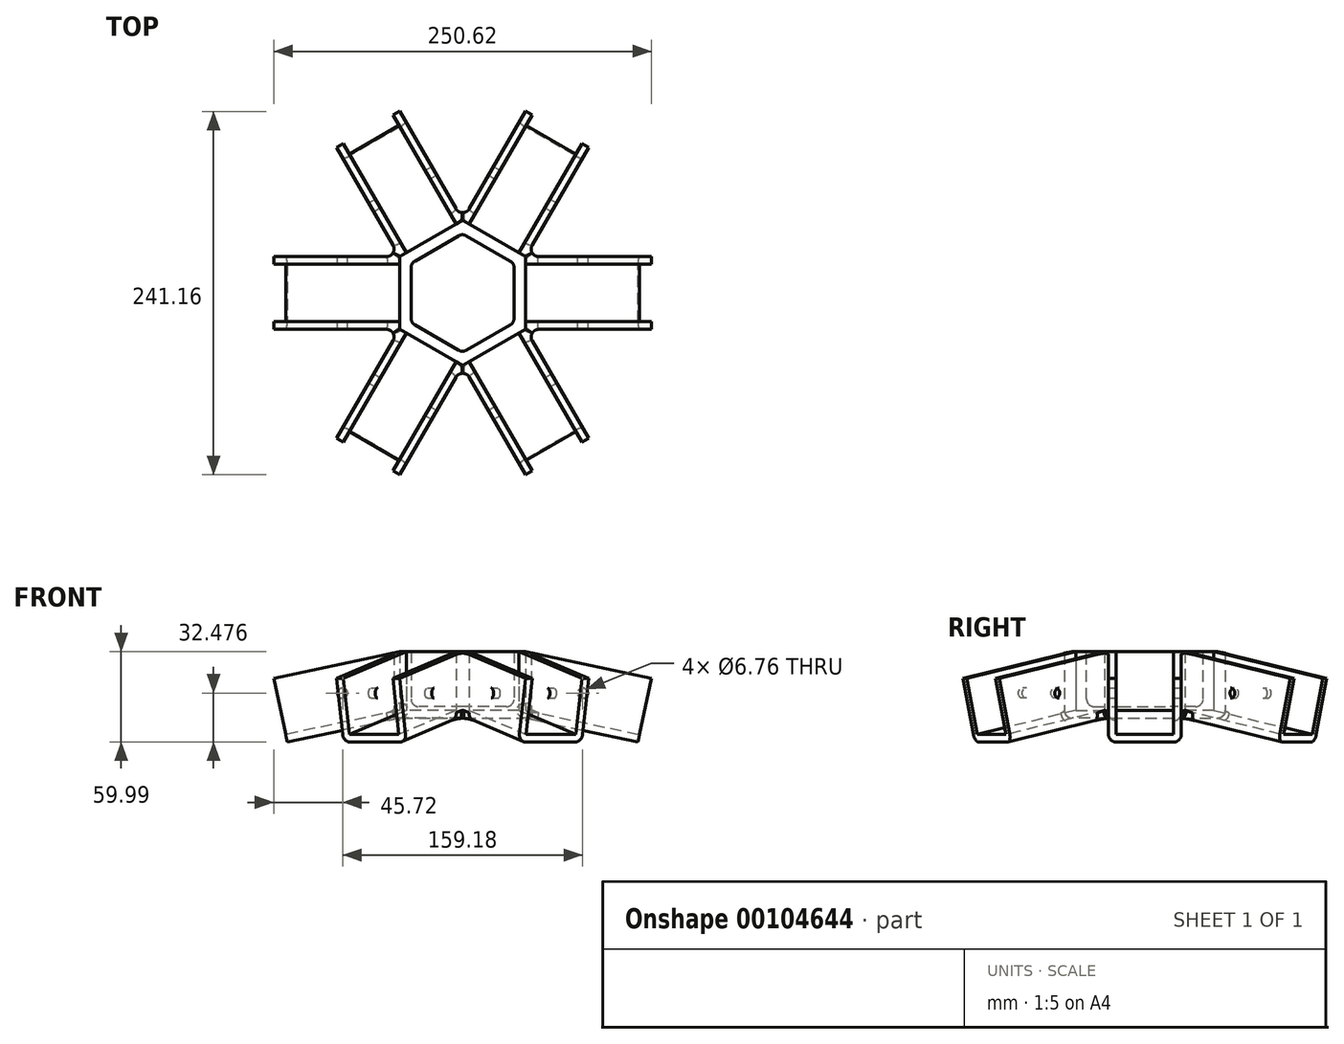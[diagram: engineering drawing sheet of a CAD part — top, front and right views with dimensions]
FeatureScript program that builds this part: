
annotation { "Feature Type Name" : "Feature", "Feature Type Description" : "" }
export const myFeature = defineFeature(function(context is Context, id is Id, definition is map)
    precondition{}
    {
        {
            var Q0;
            Q0=qCreatedBy(makeId("Top.planeOp"),FACE);
            var sketch = newSketch(context, id + "F0", { "sketchPlane" : qUnion([Q0])});
            skCircle(sketch, "E0.cCircle", {"center": v(0, 0) * mm, "radius": 41.8 * mm, "construction": true});
            skLineSegment(sketch, "E0.0", {"start": v(41.8, 24.13) * mm, "end": v(41.8, -24.13) * mm});
            skLineSegment(sketch, "E0.1", {"start": v(41.8, -24.13) * mm, "end": v(0, -48.26) * mm});
            skLineSegment(sketch, "E0.2", {"start": v(0, -48.26) * mm, "end": v(-41.8, -24.13) * mm});
            skLineSegment(sketch, "E0.3", {"start": v(-41.8, -24.13) * mm, "end": v(-41.8, 24.13) * mm});
            skLineSegment(sketch, "E0.4", {"start": v(-41.8, 24.13) * mm, "end": v(0, 48.26) * mm});
            skLineSegment(sketch, "E0.5", {"start": v(0, 48.26) * mm, "end": v(41.8, 24.13) * mm});
            skPoint(sketch, "E0.0.midPoint", {"position": v(41.8, 0) * mm});
            skSolve(sketch);
        }
        {
            var Q0;
            Q0=qSketchRegion(id+"F0",true);
            extrude(context, id + "F1", {"entities" : qUnion([Q0]), "depth" : 44.15 * mm});
        }
        {
            var Q0;
            Q0=qCreatedBy(makeId("Front.planeOp"),FACE);
            var sketch = newSketch(context, id + "F2", { "sketchPlane" : qUnion([Q0])});
            skLineSegment(sketch, "E1", {"start": v(41.8, 0) * mm, "end": v(116.33, -15.84) * mm});
            skLineSegment(sketch, "E2", {"start": v(116.33, -15.84) * mm, "end": v(125.3, 26.4) * mm});
            skLineSegment(sketch, "E3", {"start": v(125.3, 26.4) * mm, "end": v(41.8, 44.15) * mm});
            skLineSegment(sketch, "E4", {"start": v(41.8, 44.15) * mm, "end": v(41.8, 0) * mm});
            skSolve(sketch);
        }
        {
            var Q0;
            Q0=makeQuery(id+"F2.imprint","IMPRINT",FACE,{"disambiguationData":[TD([[makeQuery(id+"F2.imprint","IMPRINT",EDGE,{"derivedFrom":sQuery(id+"F2.wireOp",EDGE,"E1")}),1.0]])]});
            extrude(context, id + "F3", {"entities" : qUnion([Q0]), "endBound" : BoundingType.SYMMETRIC, "depth" : 48.26 * mm});
        }
        {
            var Q0;
            Q0=makeQuery(id+"F3.opExtrude","SWEPT_FACE",FACE,{"disambiguationData":[OSD([sQuery(id+"F2.wireOp",EDGE,"E3")])]});
            var Q1;
            Q1=makeQuery(id+"F3.opExtrude","SWEPT_FACE",FACE,{"disambiguationData":[OSD([sQuery(id+"F2.wireOp",EDGE,"E2")])]});
            var Q2;
            Q2=makeQuery(id+"F3.opExtrude","SWEPT_FACE",FACE,{"disambiguationData":[OSD([sQuery(id+"F2.wireOp",EDGE,"E4")])]});
            shell(context, id + "F4", {"entities" : qUnion([Q0, Q1, Q2]), "thickness" : 5.08 * mm});
        }
        {
            var Q0;
            Q0=makeQuery(id+"F3.opExtrude","CAP_FACE",FACE,{"disambiguationData":[OSD([sQuery(id+"F2.wireOp",EDGE,"E1"),sQuery(id+"F2.wireOp",EDGE,"E2"),sQuery(id+"F2.wireOp",EDGE,"E3"),sQuery(id+"F2.wireOp",EDGE,"E4")])],"isStart":false});
            var sketch = newSketch(context, id + "F5", { "sketchPlane" : qUnion([Q0])});
            skPoint(sketch, "E5", {"position": v(79.59, 16.64) * mm});
            skLineSegment(sketch, "E6", {"start": v(41.8, 44.15) * mm, "end": v(117.39, -10.87) * mm, "construction": true});
            skSolve(sketch);
        }
        {
            var Q0;
            Q0=sQuery(id+"F5.wireOp",VERTEX,"E5");
            var Q1;
            Q1=makeQuery(id+"F3.opExtrude","SWEPT_BODY",BODY,{"disambiguationData":[OSD([sQuery(id+"F2.wireOp",EDGE,"E1"),sQuery(id+"F2.wireOp",EDGE,"E2"),sQuery(id+"F2.wireOp",EDGE,"E3"),sQuery(id+"F2.wireOp",EDGE,"E4")])]});
            hole(context, id + "F6", {"style" : HoleStyle.SIMPLE, "endStyle" : HoleEndStyle.THROUGH, "standardTappedOrClearance" : lookupTablePath({ "standard" : "ANSI", "fit" : "Normal (ASME)", "size" : "1/4", "type" : "Clearance" }), "standardBlindInLast" : lookupTablePath({ "fit" : "Free", "standard" : "ANSI", "size" : "1/4", "type" : "Clearance" }), "holeDiameter" : 6.76 * mm, "locations" : qUnion([Q0]), "scope" : qUnion([Q1]), "isTappedThrough" : true});
        }
        {
            var Q0;
            Q0=qCreatedBy(makeId("Front.planeOp"),FACE);
            var sketch = newSketch(context, id + "F7", { "sketchPlane" : qUnion([Q0])});
            skLineSegment(sketch, "E7", {"start": v(0, 0) * mm, "end": v(0, 66.69) * mm, "construction": true});
            skSolve(sketch);
        }
        {
            var Q0;
            Q0=makeQuery(id+"F3.opExtrude","SWEPT_BODY",BODY,{"disambiguationData":[OSD([sQuery(id+"F2.wireOp",EDGE,"E1"),sQuery(id+"F2.wireOp",EDGE,"E2"),sQuery(id+"F2.wireOp",EDGE,"E3"),sQuery(id+"F2.wireOp",EDGE,"E4")])]});
            var Q1;
            Q1=sQuery(id+"F7.wireOp",EDGE,"E7");
            circularPattern(context, id + "F8", {"entities" : qUnion([Q0]), "axis" : qUnion([Q1]), "angle" : 60 * degree, "instanceCount" : 6});
        }
        {
            var Q0;
            Q0=makeQuery(id+"F1.opExtrude","CAP_FACE",FACE,{"disambiguationData":[OSD([sQuery(id+"F0.wireOp",EDGE,"E0.0"),sQuery(id+"F0.wireOp",EDGE,"E0.1"),sQuery(id+"F0.wireOp",EDGE,"E0.2"),sQuery(id+"F0.wireOp",EDGE,"E0.3"),sQuery(id+"F0.wireOp",EDGE,"E0.4"),sQuery(id+"F0.wireOp",EDGE,"E0.5")])],"isStart":false});
            shell(context, id + "F9", {"entities" : qUnion([Q0]), "thickness" : 7.62 * mm});
        }
        {
            var Q0;
            Q0=makeQuery(id+"F8.opPattern","COPY",BODY,{"derivedFrom":makeQuery(id+"F3.opExtrude","SWEPT_BODY",BODY,{"disambiguationData":[OSD([sQuery(id+"F2.wireOp",EDGE,"E1"),sQuery(id+"F2.wireOp",EDGE,"E2"),sQuery(id+"F2.wireOp",EDGE,"E3"),sQuery(id+"F2.wireOp",EDGE,"E4")])]}),"instanceName":"3"});
            var Q1;
            Q1=makeQuery(id+"F8.opPattern","COPY",BODY,{"derivedFrom":makeQuery(id+"F3.opExtrude","SWEPT_BODY",BODY,{"disambiguationData":[OSD([sQuery(id+"F2.wireOp",EDGE,"E1"),sQuery(id+"F2.wireOp",EDGE,"E2"),sQuery(id+"F2.wireOp",EDGE,"E3"),sQuery(id+"F2.wireOp",EDGE,"E4")])]}),"instanceName":"2"});
            var Q2;
            Q2=makeQuery(id+"F8.opPattern","COPY",BODY,{"derivedFrom":makeQuery(id+"F3.opExtrude","SWEPT_BODY",BODY,{"disambiguationData":[OSD([sQuery(id+"F2.wireOp",EDGE,"E1"),sQuery(id+"F2.wireOp",EDGE,"E2"),sQuery(id+"F2.wireOp",EDGE,"E3"),sQuery(id+"F2.wireOp",EDGE,"E4")])]}),"instanceName":"1"});
            var Q3;
            Q3=makeQuery(id+"F3.opExtrude","SWEPT_BODY",BODY,{"disambiguationData":[OSD([sQuery(id+"F2.wireOp",EDGE,"E1"),sQuery(id+"F2.wireOp",EDGE,"E2"),sQuery(id+"F2.wireOp",EDGE,"E3"),sQuery(id+"F2.wireOp",EDGE,"E4")])]});
            var Q4;
            Q4=makeQuery(id+"F8.opPattern","COPY",BODY,{"derivedFrom":makeQuery(id+"F3.opExtrude","SWEPT_BODY",BODY,{"disambiguationData":[OSD([sQuery(id+"F2.wireOp",EDGE,"E1"),sQuery(id+"F2.wireOp",EDGE,"E2"),sQuery(id+"F2.wireOp",EDGE,"E3"),sQuery(id+"F2.wireOp",EDGE,"E4")])]}),"instanceName":"5"});
            var Q5;
            Q5=makeQuery(id+"F8.opPattern","COPY",BODY,{"derivedFrom":makeQuery(id+"F3.opExtrude","SWEPT_BODY",BODY,{"disambiguationData":[OSD([sQuery(id+"F2.wireOp",EDGE,"E1"),sQuery(id+"F2.wireOp",EDGE,"E2"),sQuery(id+"F2.wireOp",EDGE,"E3"),sQuery(id+"F2.wireOp",EDGE,"E4")])]}),"instanceName":"4"});
            var Q6;
            Q6=makeQuery(id+"F1.opExtrude","SWEPT_BODY",BODY,{"disambiguationData":[OSD([sQuery(id+"F0.wireOp",EDGE,"E0.0"),sQuery(id+"F0.wireOp",EDGE,"E0.1"),sQuery(id+"F0.wireOp",EDGE,"E0.2"),sQuery(id+"F0.wireOp",EDGE,"E0.3"),sQuery(id+"F0.wireOp",EDGE,"E0.4"),sQuery(id+"F0.wireOp",EDGE,"E0.5")])]});
            booleanBodies(context, id + "F10", {"operationType" : BooleanOperationType.UNION, "tools" : qUnion([Q0, Q1, Q2, Q3, Q4, Q5, Q6])});
        }
        {
            var Q0;
            Q0=makeQuery(id+"F9.opShell","OFFSET_EDGE",EDGE,{"disambiguationData":[OSD([sQuery(id+"F0.wireOp",EDGE,"E0.4"),sQuery(id+"F0.wireOp",EDGE,"E0.5")])]});
            var Q1;
            Q1=makeQuery(id+"F9.opShell","OFFSET_EDGE",EDGE,{"disambiguationData":[OSD([sQuery(id+"F0.wireOp",EDGE,"E0.0"),sQuery(id+"F0.wireOp",EDGE,"E0.5")])]});
            var Q2;
            Q2=makeQuery(id+"F9.opShell","OFFSET_EDGE",EDGE,{"disambiguationData":[OSD([sQuery(id+"F0.wireOp",EDGE,"E0.0"),sQuery(id+"F0.wireOp",EDGE,"E0.1")])]});
            var Q3;
            Q3=makeQuery(id+"F9.opShell","OFFSET_EDGE",EDGE,{"disambiguationData":[OSD([sQuery(id+"F0.wireOp",EDGE,"E0.1"),sQuery(id+"F0.wireOp",EDGE,"E0.2")])]});
            var Q4;
            Q4=makeQuery(id+"F9.opShell","OFFSET_EDGE",EDGE,{"disambiguationData":[OSD([sQuery(id+"F0.wireOp",EDGE,"E0.2"),sQuery(id+"F0.wireOp",EDGE,"E0.3")])]});
            var Q5;
            Q5=makeQuery(id+"F9.opShell","OFFSET_EDGE",EDGE,{"disambiguationData":[OSD([sQuery(id+"F0.wireOp",EDGE,"E0.3"),sQuery(id+"F0.wireOp",EDGE,"E0.4")])]});
            fillet(context, id + "F11", {"entities" : qUnion([Q0, Q1, Q2, Q3, Q4, Q5]), "radius" : 5.08 * mm, "tangentPropagation" : true, "allowEdgeOverflow" : false});
        }
        {
            var Q0;
            {var subQ0=sQuery(id+"F2.wireOp",EDGE,"E4");Q0=makeQuery(id+"F10.opBoolean","MERGE",EDGE,{"derivedFrom":[makeQuery(id+"F1.opExtrude","SWEPT_EDGE",EDGE,{"disambiguationData":[OSD([sQuery(id+"F0.wireOp",EDGE,"E0.1"),sQuery(id+"F0.wireOp",EDGE,"E0.2")])]}),makeQuery(id+"F8.opPattern","COPY",EDGE,{"derivedFrom":makeQuery(id+"F3.opExtrude","CAP_EDGE",EDGE,{"disambiguationData":[OSD([subQ0])],"isStart":true}),"instanceName":"4"}),makeQuery(id+"F8.opPattern","COPY",EDGE,{"derivedFrom":makeQuery(id+"F3.opExtrude","CAP_EDGE",EDGE,{"disambiguationData":[OSD([subQ0])],"isStart":false}),"instanceName":"5"})]});}
            var Q1;
            {var subQ0=sQuery(id+"F2.wireOp",EDGE,"E4");Q1=makeQuery(id+"F10.opBoolean","MERGE",EDGE,{"derivedFrom":[makeQuery(id+"F1.opExtrude","SWEPT_EDGE",EDGE,{"disambiguationData":[OSD([sQuery(id+"F0.wireOp",EDGE,"E0.0"),sQuery(id+"F0.wireOp",EDGE,"E0.1")])]}),makeQuery(id+"F3.opExtrude","CAP_EDGE",EDGE,{"disambiguationData":[OSD([subQ0])],"isStart":false}),makeQuery(id+"F8.opPattern","COPY",EDGE,{"derivedFrom":makeQuery(id+"F3.opExtrude","CAP_EDGE",EDGE,{"disambiguationData":[OSD([subQ0])],"isStart":true}),"instanceName":"5"})]});}
            var Q2;
            {var subQ0=sQuery(id+"F2.wireOp",EDGE,"E4");Q2=makeQuery(id+"F10.opBoolean","MERGE",EDGE,{"derivedFrom":[makeQuery(id+"F1.opExtrude","SWEPT_EDGE",EDGE,{"disambiguationData":[OSD([sQuery(id+"F0.wireOp",EDGE,"E0.0"),sQuery(id+"F0.wireOp",EDGE,"E0.5")])]}),makeQuery(id+"F3.opExtrude","CAP_EDGE",EDGE,{"disambiguationData":[OSD([subQ0])],"isStart":true}),makeQuery(id+"F8.opPattern","COPY",EDGE,{"derivedFrom":makeQuery(id+"F3.opExtrude","CAP_EDGE",EDGE,{"disambiguationData":[OSD([subQ0])],"isStart":false}),"instanceName":"1"})]});}
            var Q3;
            {var subQ0=sQuery(id+"F2.wireOp",EDGE,"E4");Q3=makeQuery(id+"F10.opBoolean","MERGE",EDGE,{"derivedFrom":[makeQuery(id+"F1.opExtrude","SWEPT_EDGE",EDGE,{"disambiguationData":[OSD([sQuery(id+"F0.wireOp",EDGE,"E0.4"),sQuery(id+"F0.wireOp",EDGE,"E0.5")])]}),makeQuery(id+"F8.opPattern","COPY",EDGE,{"derivedFrom":makeQuery(id+"F3.opExtrude","CAP_EDGE",EDGE,{"disambiguationData":[OSD([subQ0])],"isStart":true}),"instanceName":"1"}),makeQuery(id+"F8.opPattern","COPY",EDGE,{"derivedFrom":makeQuery(id+"F3.opExtrude","CAP_EDGE",EDGE,{"disambiguationData":[OSD([subQ0])],"isStart":false}),"instanceName":"2"})]});}
            var Q4;
            {var subQ0=sQuery(id+"F2.wireOp",EDGE,"E4");Q4=makeQuery(id+"F10.opBoolean","MERGE",EDGE,{"derivedFrom":[makeQuery(id+"F1.opExtrude","SWEPT_EDGE",EDGE,{"disambiguationData":[OSD([sQuery(id+"F0.wireOp",EDGE,"E0.3"),sQuery(id+"F0.wireOp",EDGE,"E0.4")])]}),makeQuery(id+"F8.opPattern","COPY",EDGE,{"derivedFrom":makeQuery(id+"F3.opExtrude","CAP_EDGE",EDGE,{"disambiguationData":[OSD([subQ0])],"isStart":true}),"instanceName":"2"}),makeQuery(id+"F8.opPattern","COPY",EDGE,{"derivedFrom":makeQuery(id+"F3.opExtrude","CAP_EDGE",EDGE,{"disambiguationData":[OSD([subQ0])],"isStart":false}),"instanceName":"3"})]});}
            var Q5;
            {var subQ0=sQuery(id+"F2.wireOp",EDGE,"E4");Q5=makeQuery(id+"F10.opBoolean","MERGE",EDGE,{"derivedFrom":[makeQuery(id+"F1.opExtrude","SWEPT_EDGE",EDGE,{"disambiguationData":[OSD([sQuery(id+"F0.wireOp",EDGE,"E0.2"),sQuery(id+"F0.wireOp",EDGE,"E0.3")])]}),makeQuery(id+"F8.opPattern","COPY",EDGE,{"derivedFrom":makeQuery(id+"F3.opExtrude","CAP_EDGE",EDGE,{"disambiguationData":[OSD([subQ0])],"isStart":true}),"instanceName":"3"}),makeQuery(id+"F8.opPattern","COPY",EDGE,{"derivedFrom":makeQuery(id+"F3.opExtrude","CAP_EDGE",EDGE,{"disambiguationData":[OSD([subQ0])],"isStart":false}),"instanceName":"4"})]});}
            fillet(context, id + "F12", {"entities" : qUnion([Q0, Q1, Q2, Q3, Q4, Q5]), "radius" : 5.08 * mm, "tangentPropagation" : true, "allowEdgeOverflow" : false});
        }
        {
            var Q0;
            {var subQ0=sQuery(id+"F0.wireOp",EDGE,"E0.3");Q0=makeQuery(id+"F9.opShell","OFFSET_EDGE",EDGE,{"disambiguationData":[OSD([subQ0]),TDD([makeQuery(id+"F1.opExtrude","CAP_EDGE",EDGE,{"disambiguationData":[OSD([subQ0])],"isStart":true})])]});}
            fillet(context, id + "F13", {"entities" : qUnion([Q0]), "radius" : 5.08 * mm, "tangentPropagation" : true, "allowEdgeOverflow" : false});
        }
        {
            var Q0;
            Q0=makeQuery(id+"F8.opPattern","COPY",EDGE,{"derivedFrom":makeQuery(id+"F3.opExtrude","CAP_EDGE",EDGE,{"disambiguationData":[OSD([sQuery(id+"F2.wireOp",EDGE,"E1")])],"isStart":false}),"instanceName":"1"});
            var Q1;
            Q1=makeQuery(id+"F3.opExtrude","CAP_EDGE",EDGE,{"disambiguationData":[OSD([sQuery(id+"F2.wireOp",EDGE,"E1")])],"isStart":true});
            var Q2;
            Q2=makeQuery(id+"F8.opPattern","COPY",EDGE,{"derivedFrom":makeQuery(id+"F3.opExtrude","CAP_EDGE",EDGE,{"disambiguationData":[OSD([sQuery(id+"F2.wireOp",EDGE,"E1")])],"isStart":true}),"instanceName":"1"});
            var Q3;
            Q3=makeQuery(id+"F8.opPattern","COPY",EDGE,{"derivedFrom":makeQuery(id+"F3.opExtrude","CAP_EDGE",EDGE,{"disambiguationData":[OSD([sQuery(id+"F2.wireOp",EDGE,"E1")])],"isStart":false}),"instanceName":"2"});
            var Q4;
            Q4=makeQuery(id+"F8.opPattern","COPY",EDGE,{"derivedFrom":makeQuery(id+"F3.opExtrude","CAP_EDGE",EDGE,{"disambiguationData":[OSD([sQuery(id+"F2.wireOp",EDGE,"E1")])],"isStart":true}),"instanceName":"2"});
            var Q5;
            Q5=makeQuery(id+"F8.opPattern","COPY",EDGE,{"derivedFrom":makeQuery(id+"F3.opExtrude","CAP_EDGE",EDGE,{"disambiguationData":[OSD([sQuery(id+"F2.wireOp",EDGE,"E1")])],"isStart":false}),"instanceName":"3"});
            var Q6;
            Q6=makeQuery(id+"F8.opPattern","COPY",EDGE,{"derivedFrom":makeQuery(id+"F3.opExtrude","CAP_EDGE",EDGE,{"disambiguationData":[OSD([sQuery(id+"F2.wireOp",EDGE,"E1")])],"isStart":true}),"instanceName":"3"});
            var Q7;
            Q7=makeQuery(id+"F8.opPattern","COPY",EDGE,{"derivedFrom":makeQuery(id+"F3.opExtrude","CAP_EDGE",EDGE,{"disambiguationData":[OSD([sQuery(id+"F2.wireOp",EDGE,"E1")])],"isStart":false}),"instanceName":"4"});
            var Q8;
            Q8=makeQuery(id+"F8.opPattern","COPY",EDGE,{"derivedFrom":makeQuery(id+"F3.opExtrude","CAP_EDGE",EDGE,{"disambiguationData":[OSD([sQuery(id+"F2.wireOp",EDGE,"E1")])],"isStart":true}),"instanceName":"4"});
            var Q9;
            Q9=makeQuery(id+"F8.opPattern","COPY",EDGE,{"derivedFrom":makeQuery(id+"F3.opExtrude","CAP_EDGE",EDGE,{"disambiguationData":[OSD([sQuery(id+"F2.wireOp",EDGE,"E1")])],"isStart":false}),"instanceName":"5"});
            var Q10;
            Q10=makeQuery(id+"F3.opExtrude","CAP_EDGE",EDGE,{"disambiguationData":[OSD([sQuery(id+"F2.wireOp",EDGE,"E1")])],"isStart":false});
            var Q11;
            Q11=makeQuery(id+"F8.opPattern","COPY",EDGE,{"derivedFrom":makeQuery(id+"F3.opExtrude","CAP_EDGE",EDGE,{"disambiguationData":[OSD([sQuery(id+"F2.wireOp",EDGE,"E1")])],"isStart":true}),"instanceName":"5"});
            fillet(context, id + "F14", {"entities" : qUnion([Q0, Q1, Q2, Q3, Q4, Q5, Q6, Q7, Q8, Q9, Q10, Q11]), "radius" : 5.08 * mm, "tangentPropagation" : true, "allowEdgeOverflow" : false});
        }
    });
